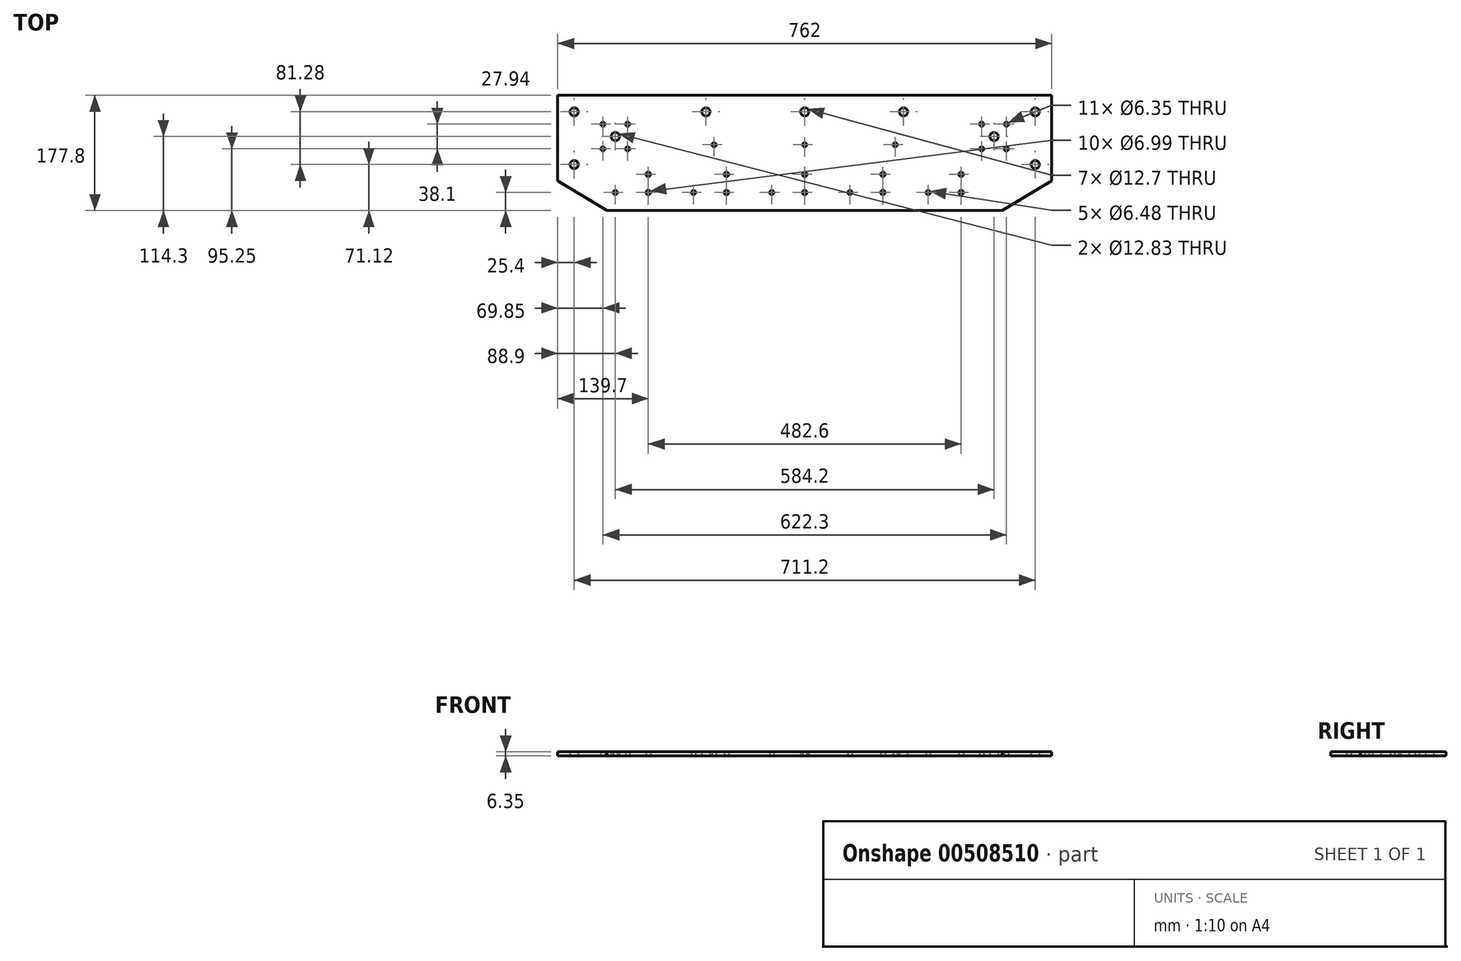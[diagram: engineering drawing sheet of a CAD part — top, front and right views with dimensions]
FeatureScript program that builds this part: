
annotation { "Feature Type Name" : "Feature", "Feature Type Description" : "" }
export const myFeature = defineFeature(function(context is Context, id is Id, definition is map)
    precondition{}
    {
        {
            var Q0;
            Q0=qCreatedBy(makeId("Top.planeOp"),FACE);
            var sketch = newSketch(context, id + "F0", { "sketchPlane" : qUnion([Q0])});
            skLineSegment(sketch, "E0.bottom", {"start": v(0, 0) * mm, "end": v(762, 0) * mm});
            skLineSegment(sketch, "E0.top", {"start": v(76.2, -177.8) * mm, "end": v(685.8, -177.8) * mm});
            skLineSegment(sketch, "E0.left", {"start": v(0, 0) * mm, "end": v(0, -132.08) * mm});
            skLineSegment(sketch, "E0.right", {"start": v(762, 0) * mm, "end": v(762, -132.08) * mm});
            skLineSegment(sketch, "E1", {"start": v(0, -132.08) * mm, "end": v(76.2, -177.8) * mm});
            skLineSegment(sketch, "E2", {"start": v(762, -132.08) * mm, "end": v(685.8, -177.8) * mm});
            skPoint(sketch, "E3.orphan", {"position": v(762, -177.8) * mm});
            skPoint(sketch, "E4.orphan", {"position": v(0, -177.8) * mm});
            skLineSegment(sketch, "E5", {"start": v(0, -63.5) * mm, "end": v(762, -63.5) * mm, "construction": true});
            skLineSegment(sketch, "E6", {"start": v(0, -121.92) * mm, "end": v(762, -121.92) * mm, "construction": true});
            skCircle(sketch, "E7", {"center": v(88.9, -63.5) * mm, "radius": 6.41 * mm});
            skCircle(sketch, "E8", {"center": v(673.1, -63.5) * mm, "radius": 6.41 * mm});
            skLineSegment(sketch, "E9", {"start": v(139.7, -121.92) * mm, "end": v(139.7, -177.8) * mm, "construction": true});
            skLineSegment(sketch, "E10", {"start": v(622.3, -121.92) * mm, "end": v(622.3, -177.8) * mm, "construction": true});
            skLineSegment(sketch, "E11", {"start": v(260.35, -121.92) * mm, "end": v(260.35, -177.8) * mm, "construction": true});
            skLineSegment(sketch, "E12", {"start": v(501.65, -121.92) * mm, "end": v(501.65, -177.8) * mm, "construction": true});
            skLineSegment(sketch, "E13", {"start": v(381, -121.92) * mm, "end": v(381, -177.8) * mm, "construction": true});
            skCircle(sketch, "E14", {"center": v(139.7, -121.92) * mm, "radius": 3.5 * mm});
            skCircle(sketch, "E15", {"center": v(260.35, -121.92) * mm, "radius": 3.5 * mm});
            skCircle(sketch, "E16", {"center": v(381, -121.92) * mm, "radius": 3.5 * mm});
            skCircle(sketch, "E17", {"center": v(501.65, -121.92) * mm, "radius": 3.5 * mm});
            skCircle(sketch, "E18", {"center": v(622.3, -121.92) * mm, "radius": 3.5 * mm});
            skLineSegment(sketch, "E19", {"start": v(88.9, -76.2) * mm, "end": v(673.1, -76.2) * mm, "construction": true});
            skLineSegment(sketch, "E20", {"start": v(88.9, -63.5) * mm, "end": v(88.9, -76.2) * mm, "construction": true});
            skLineSegment(sketch, "E21", {"start": v(673.1, -63.5) * mm, "end": v(673.1, -76.2) * mm, "construction": true});
            skCircle(sketch, "E22", {"center": v(381, -76.2) * mm, "radius": 3.18 * mm});
            skCircle(sketch, "E23", {"center": v(241.3, -76.2) * mm, "radius": 3.18 * mm});
            skCircle(sketch, "E24", {"center": v(520.7, -76.2) * mm, "radius": 3.18 * mm});
            skCircle(sketch, "E25", {"center": v(139.7, -149.86) * mm, "radius": 3.5 * mm});
            skCircle(sketch, "E26", {"center": v(260.35, -149.86) * mm, "radius": 3.5 * mm});
            skCircle(sketch, "E27", {"center": v(381, -149.86) * mm, "radius": 3.5 * mm});
            skCircle(sketch, "E28", {"center": v(501.65, -149.86) * mm, "radius": 3.5 * mm});
            skCircle(sketch, "E29", {"center": v(622.3, -149.86) * mm, "radius": 3.5 * mm});
            skCircle(sketch, "E30", {"center": v(25.4, -25.4) * mm, "radius": 6.35 * mm});
            skCircle(sketch, "E31", {"center": v(736.6, -25.4) * mm, "radius": 6.35 * mm});
            skLineSegment(sketch, "E32", {"start": v(25.4, -25.4) * mm, "end": v(736.6, -25.4) * mm, "construction": true});
            skCircle(sketch, "E33", {"center": v(381, -25.4) * mm, "radius": 6.35 * mm});
            skCircle(sketch, "E34", {"center": v(533.4, -25.4) * mm, "radius": 6.35 * mm});
            skCircle(sketch, "E35", {"center": v(228.6, -25.4) * mm, "radius": 6.35 * mm});
            skCircle(sketch, "E36", {"center": v(25.4, -106.68) * mm, "radius": 6.35 * mm});
            skCircle(sketch, "E37", {"center": v(736.6, -106.68) * mm, "radius": 6.35 * mm});
            skLineSegment(sketch, "E38", {"start": v(88.9, -149.86) * mm, "end": v(647.9, -149.86) * mm, "construction": true});
            skCircle(sketch, "E39", {"center": v(209.55, -149.86) * mm, "radius": 3.24 * mm});
            skCircle(sketch, "E40", {"center": v(330.2, -149.86) * mm, "radius": 3.24 * mm});
            skCircle(sketch, "E41", {"center": v(450.85, -149.86) * mm, "radius": 3.24 * mm});
            skCircle(sketch, "E42", {"center": v(571.5, -149.86) * mm, "radius": 3.24 * mm});
            skCircle(sketch, "E43", {"center": v(88.9, -149.86) * mm, "radius": 3.24 * mm});
            skLineSegment(sketch, "E44.bottom", {"start": v(69.85, -44.45) * mm, "end": v(107.95, -44.45) * mm, "construction": true});
            skLineSegment(sketch, "E44.top", {"start": v(69.85, -82.55) * mm, "end": v(107.95, -82.55) * mm, "construction": true});
            skLineSegment(sketch, "E44.left", {"start": v(69.85, -44.45) * mm, "end": v(69.85, -82.55) * mm, "construction": true});
            skLineSegment(sketch, "E44.right", {"start": v(107.95, -44.45) * mm, "end": v(107.95, -82.55) * mm, "construction": true});
            skCircle(sketch, "E45", {"center": v(107.95, -44.45) * mm, "radius": 3.18 * mm});
            skCircle(sketch, "E46", {"center": v(69.85, -44.45) * mm, "radius": 3.18 * mm});
            skCircle(sketch, "E47", {"center": v(69.85, -82.55) * mm, "radius": 3.18 * mm});
            skCircle(sketch, "E48", {"center": v(107.95, -82.55) * mm, "radius": 3.18 * mm});
            skLineSegment(sketch, "E49.bottom", {"start": v(654.05, -44.45) * mm, "end": v(692.15, -44.45) * mm, "construction": true});
            skLineSegment(sketch, "E49.top", {"start": v(654.05, -82.55) * mm, "end": v(692.15, -82.55) * mm, "construction": true});
            skLineSegment(sketch, "E49.left", {"start": v(654.05, -44.45) * mm, "end": v(654.05, -82.55) * mm, "construction": true});
            skLineSegment(sketch, "E49.right", {"start": v(692.15, -44.45) * mm, "end": v(692.15, -82.55) * mm, "construction": true});
            skCircle(sketch, "E50", {"center": v(654.05, -44.45) * mm, "radius": 3.18 * mm});
            skCircle(sketch, "E51", {"center": v(692.15, -44.45) * mm, "radius": 3.18 * mm});
            skCircle(sketch, "E52", {"center": v(692.15, -82.55) * mm, "radius": 3.18 * mm});
            skCircle(sketch, "E53", {"center": v(654.05, -82.55) * mm, "radius": 3.18 * mm});
            skSolve(sketch);
        }
        {
            var Q0;
            Q0=makeQuery(id+"F0.imprint","IMPRINT",FACE,{"disambiguationData":[TD([[makeQuery(id+"F0.imprint","IMPRINT",EDGE,{"derivedFrom":sQuery(id+"F0.wireOp",EDGE,"E0.bottom")}),-1.0]])]});
            extrude(context, id + "F1", {"entities" : qUnion([Q0]), "depth" : 6.35 * mm});
        }
    });
